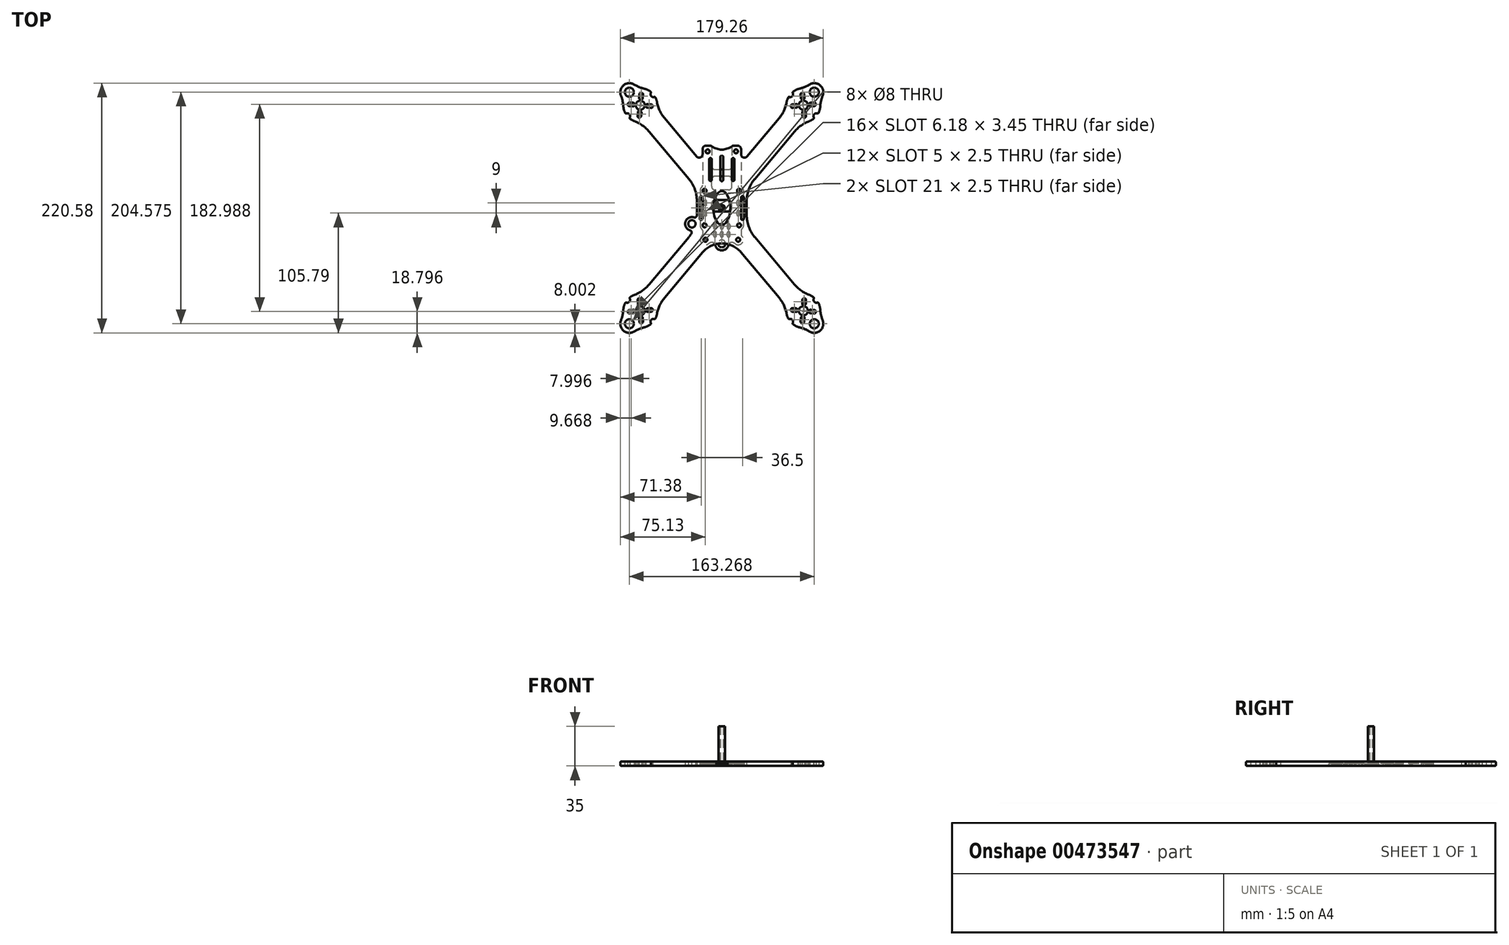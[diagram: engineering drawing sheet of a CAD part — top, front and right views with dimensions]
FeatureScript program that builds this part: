
annotation { "Feature Type Name" : "Feature", "Feature Type Description" : "" }
export const myFeature = defineFeature(function(context is Context, id is Id, definition is map)
    precondition{}
    {
        {
            var Q0;
            Q0=qCreatedBy(makeId("Top.planeOp"),FACE);
            var sketch = newSketch(context, id + "F0", { "sketchPlane" : qUnion([Q0])});
            skCircle(sketch, "E0", {"center": v(-72, 90.8) * mm, "radius": 64.25 * mm, "construction": true});
            skLineSegment(sketch, "E1", {"start": v(-72, 90.8) * mm, "end": v(0, 5) * mm, "construction": true});
            skCircle(sketch, "E2", {"center": v(-72, 90.8) * mm, "radius": 4 * mm});
            skArc(sketch, "E3", {"start": v(-86.97, 89.92) * mm, "mid": v(-86.48, 86.9) * mm, "end": v(-85.4, 84.06) * mm});
            skArc(sketch, "E4", {"start": v(-77.42, 109.09) * mm, "mid": v(-86.78, 108.42) * mm, "end": v(-89.06, 99.32) * mm});
            skLineSegment(sketch, "E5", {"start": v(-81.63, 102.29) * mm, "end": v(-72, 90.8) * mm, "construction": true});
            skPoint(sketch, "E6.visualSharp", {"position": v(-74.36, 105.6) * mm});
            skArc(sketch, "E6.filletArc", {"start": v(-77.42, 109.09) * mm, "mid": v(-73.12, 106.88) * mm, "end": v(-68.53, 105.4) * mm});
            skArc(sketch, "E7.MirrorCS", {"start": v(-89.06, 99.32) * mm, "mid": v(-87.64, 94.7) * mm, "end": v(-86.97, 89.92) * mm});
            skCircle(sketch, "E8", {"center": v(-81.63, 102.29) * mm, "radius": 4 * mm});
            skLineSegment(sketch, "E9", {"start": v(-72, 90.8) * mm, "end": v(-60.5, 100.44) * mm, "construction": true});
            skArc(sketch, "E10", {"start": v(-62.73, 101.57) * mm, "mid": v(-62.42, 98.83) * mm, "end": v(-59.78, 98.05) * mm});
            skArc(sketch, "E11.trimOffspring", {"start": v(-63.03, 102.82) * mm, "mid": v(-65.65, 104.39) * mm, "end": v(-68.53, 105.4) * mm});
            skArc(sketch, "E12.MirrorCS", {"start": v(-84.2, 83.55) * mm, "mid": v(-81.57, 82.76) * mm, "end": v(-81.25, 80.03) * mm});
            skArc(sketch, "E13.trimOffspring", {"start": v(-80.96, 78.77) * mm, "mid": v(-79.2, 77.64) * mm, "end": v(-77.3, 76.77) * mm});
            skPoint(sketch, "E14.visualSharp", {"position": v(-62.26, 102.21) * mm});
            skArc(sketch, "E14.filletArc", {"start": v(-62.73, 101.57) * mm, "mid": v(-62.65, 102.25) * mm, "end": v(-63.03, 102.82) * mm});
            skPoint(sketch, "E15.visualSharp", {"position": v(-59.06, 98.4) * mm});
            skArc(sketch, "E15.filletArc", {"start": v(-58.6, 97.54) * mm, "mid": v(-59.1, 98) * mm, "end": v(-59.78, 98.05) * mm});
            skPoint(sketch, "E16.visualSharp", {"position": v(-84.92, 83.2) * mm});
            skArc(sketch, "E16.filletArc", {"start": v(-85.4, 84.06) * mm, "mid": v(-84.9, 83.59) * mm, "end": v(-84.2, 83.55) * mm});
            skPoint(sketch, "E17.visualSharp", {"position": v(-81.72, 79.38) * mm});
            skArc(sketch, "E17.filletArc", {"start": v(-81.25, 80.03) * mm, "mid": v(-81.33, 79.34) * mm, "end": v(-80.96, 78.77) * mm});
            skCircle(sketch, "E18", {"center": v(-15.25, 15.25) * mm, "radius": 1.75 * mm});
            skCircle(sketch, "E19", {"center": v(-12.5, 50) * mm, "radius": 1.75 * mm});
            skLineSegment(sketch, "E20", {"start": v(-14, 55) * mm, "end": v(-10.52, 55) * mm});
            skArc(sketch, "E21", {"start": v(-8.76, 54.43) * mm, "mid": v(-4.6, 52.33) * mm, "end": v(0, 51.6) * mm});
            skLineSegment(sketch, "E22.bottom", {"start": v(-18.25, 10.5) * mm, "end": v(-18.25, 10.5) * mm});
            skLineSegment(sketch, "E22.top", {"start": v(-19.5, 0) * mm, "end": v(-17, 0) * mm, "construction": true});
            skLineSegment(sketch, "E22.left", {"start": v(-19.5, 9.25) * mm, "end": v(-19.5, 0) * mm});
            skLineSegment(sketch, "E22.right", {"start": v(-17, 9.25) * mm, "end": v(-17, 0) * mm});
            skLineSegment(sketch, "E23", {"start": v(0, 51.6) * mm, "end": v(0, 0) * mm, "construction": true});
            skPoint(sketch, "E24.visualSharp", {"position": v(-9.5, 55) * mm});
            skArc(sketch, "E24.filletArc", {"start": v(-8.76, 54.43) * mm, "mid": v(-9.6, 54.86) * mm, "end": v(-10.52, 55) * mm});
            skLineSegment(sketch, "E25", {"start": v(-64.12, 67.4) * mm, "end": v(-29.02, 25.58) * mm});
            skLineSegment(sketch, "E26.MirrorCS", {"start": v(-50.67, 79.38) * mm, "end": v(-22.3, 45.58) * mm});
            skArc(sketch, "E27.trimOffspring", {"start": v(-57.22, 93.42) * mm, "mid": v(-57.76, 95.53) * mm, "end": v(-58.6, 97.54) * mm});
            skPoint(sketch, "E28.visualSharp", {"position": v(-57.38, 87.39) * mm});
            skArc(sketch, "E28.filletArc", {"start": v(-57.22, 93.42) * mm, "mid": v(-54.87, 85.97) * mm, "end": v(-50.67, 79.38) * mm});
            skPoint(sketch, "E29.visualSharp", {"position": v(-71.17, 75.82) * mm});
            skArc(sketch, "E29.filletArc", {"start": v(-64.12, 67.4) * mm, "mid": v(-70.1, 72.94) * mm, "end": v(-77.3, 76.77) * mm});
            skLineSegment(sketch, "E30", {"start": v(-17, 52) * mm, "end": v(-17, 47.5) * mm});
            skPoint(sketch, "E31.visualSharp", {"position": v(-17, 55) * mm});
            skArc(sketch, "E31.filletArc", {"start": v(-14, 55) * mm, "mid": v(-16.12, 54.12) * mm, "end": v(-17, 52) * mm});
            skPoint(sketch, "E32.visualSharp", {"position": v(-17, 39.26) * mm});
            skArc(sketch, "E32.filletArc", {"start": v(-22.3, 45.58) * mm, "mid": v(-18.97, 44.68) * mm, "end": v(-17, 47.5) * mm});
            skLineSegment(sketch, "E33", {"start": v(-22, 6.3) * mm, "end": v(-22, 0) * mm});
            skPoint(sketch, "E34.visualSharp", {"position": v(-22, 17.22) * mm});
            skArc(sketch, "E34.filletArc", {"start": v(-22, 6.3) * mm, "mid": v(-23.8, 16.56) * mm, "end": v(-29.02, 25.58) * mm});
            skPoint(sketch, "E35.visualSharp", {"position": v(-19.5, 10.5) * mm});
            skArc(sketch, "E35.filletArc", {"start": v(-18.25, 10.5) * mm, "mid": v(-19.13, 10.13) * mm, "end": v(-19.5, 9.25) * mm});
            skPoint(sketch, "E36.visualSharp", {"position": v(-17, 10.5) * mm});
            skArc(sketch, "E36.filletArc", {"start": v(-17, 9.25) * mm, "mid": v(-17.37, 10.13) * mm, "end": v(-18.25, 10.5) * mm});
            skCircle(sketch, "E37.MirrorC", {"center": v(12.5, 50) * mm, "radius": 1.75 * mm});
            skCircle(sketch, "E38.MirrorC", {"center": v(15.25, 15.25) * mm, "radius": 1.75 * mm});
            skArc(sketch, "E39.MirrorCS", {"start": v(17, 9.25) * mm, "mid": v(17.37, 10.13) * mm, "end": v(18.25, 10.5) * mm});
            skArc(sketch, "E40.MirrorCS", {"start": v(18.25, 10.5) * mm, "mid": v(19.13, 10.13) * mm, "end": v(19.5, 9.25) * mm});
            skLineSegment(sketch, "E41.MirrorCS", {"start": v(18.25, 10.5) * mm, "end": v(18.25, 10.5) * mm});
            skPoint(sketch, "E42.MirrorP", {"position": v(17, 10.5) * mm});
            skPoint(sketch, "E43.MirrorP", {"position": v(19.5, 10.5) * mm});
            skLineSegment(sketch, "E44.MirrorCS", {"start": v(17, 9.25) * mm, "end": v(17, 0) * mm});
            skLineSegment(sketch, "E45.MirrorCS", {"start": v(19.5, 9.25) * mm, "end": v(19.5, 0) * mm});
            skArc(sketch, "E46.MirrorCS", {"start": v(22, 6.3) * mm, "mid": v(23.8, 16.56) * mm, "end": v(29.02, 25.58) * mm});
            skLineSegment(sketch, "E47.MirrorCS", {"start": v(22, 6.3) * mm, "end": v(22, 0) * mm});
            skLineSegment(sketch, "E48.MirrorCS", {"start": v(50.67, 79.38) * mm, "end": v(22.3, 45.58) * mm});
            skLineSegment(sketch, "E49.MirrorCS", {"start": v(64.12, 67.4) * mm, "end": v(29.02, 25.58) * mm});
            skArc(sketch, "E50.MirrorCS", {"start": v(57.22, 93.42) * mm, "mid": v(54.87, 85.97) * mm, "end": v(50.67, 79.38) * mm});
            skArc(sketch, "E51.MirrorCS", {"start": v(64.12, 67.4) * mm, "mid": v(70.1, 72.94) * mm, "end": v(77.3, 76.77) * mm});
            skArc(sketch, "E52.MirrorCS", {"start": v(80.96, 78.77) * mm, "mid": v(79.2, 77.64) * mm, "end": v(77.3, 76.77) * mm});
            skArc(sketch, "E53.MirrorCS", {"start": v(57.22, 93.42) * mm, "mid": v(57.76, 95.53) * mm, "end": v(58.6, 97.54) * mm});
            skArc(sketch, "E54.MirrorCS", {"start": v(84.2, 83.55) * mm, "mid": v(81.57, 82.76) * mm, "end": v(81.25, 80.03) * mm});
            skArc(sketch, "E55.MirrorCS", {"start": v(85.4, 84.06) * mm, "mid": v(84.9, 83.59) * mm, "end": v(84.2, 83.55) * mm});
            skArc(sketch, "E56.MirrorCS", {"start": v(81.25, 80.03) * mm, "mid": v(81.33, 79.34) * mm, "end": v(80.96, 78.77) * mm});
            skArc(sketch, "E57.MirrorCS", {"start": v(86.97, 89.92) * mm, "mid": v(86.48, 86.9) * mm, "end": v(85.4, 84.06) * mm});
            skArc(sketch, "E58.MirrorCS", {"start": v(89.06, 99.32) * mm, "mid": v(87.64, 94.7) * mm, "end": v(86.97, 89.92) * mm});
            skArc(sketch, "E59.MirrorCS", {"start": v(77.42, 109.09) * mm, "mid": v(86.78, 108.42) * mm, "end": v(89.06, 99.32) * mm});
            skArc(sketch, "E60.MirrorCS", {"start": v(77.42, 109.09) * mm, "mid": v(73.12, 106.88) * mm, "end": v(68.53, 105.4) * mm});
            skArc(sketch, "E61.MirrorCS", {"start": v(63.03, 102.82) * mm, "mid": v(65.65, 104.39) * mm, "end": v(68.53, 105.4) * mm});
            skArc(sketch, "E62.MirrorCS", {"start": v(62.73, 101.57) * mm, "mid": v(62.65, 102.25) * mm, "end": v(63.03, 102.82) * mm});
            skArc(sketch, "E63.MirrorCS", {"start": v(62.73, 101.57) * mm, "mid": v(62.42, 98.83) * mm, "end": v(59.78, 98.05) * mm});
            skPoint(sketch, "E64.MirrorP", {"position": v(59.06, 98.4) * mm});
            skArc(sketch, "E65.MirrorCS", {"start": v(58.6, 97.54) * mm, "mid": v(59.1, 98) * mm, "end": v(59.78, 98.05) * mm});
            skCircle(sketch, "E66.MirrorC", {"center": v(81.63, 102.29) * mm, "radius": 4 * mm});
            skCircle(sketch, "E67.MirrorC", {"center": v(72, 90.8) * mm, "radius": 4 * mm});
            skArc(sketch, "E68.MirrorCS", {"start": v(22.3, 45.58) * mm, "mid": v(18.97, 44.68) * mm, "end": v(17, 47.5) * mm});
            skLineSegment(sketch, "E69.MirrorCS", {"start": v(17, 52) * mm, "end": v(17, 47.5) * mm});
            skArc(sketch, "E70.MirrorCS", {"start": v(14, 55) * mm, "mid": v(16.12, 54.12) * mm, "end": v(17, 52) * mm});
            skLineSegment(sketch, "E71.MirrorCS", {"start": v(14, 55) * mm, "end": v(10.52, 55) * mm});
            skArc(sketch, "E72.MirrorCS", {"start": v(8.76, 54.43) * mm, "mid": v(9.6, 54.86) * mm, "end": v(10.52, 55) * mm});
            skArc(sketch, "E73.MirrorCS", {"start": v(8.76, 54.43) * mm, "mid": v(4.6, 52.33) * mm, "end": v(0, 51.6) * mm});
            skArc(sketch, "E74.MirrorCS", {"start": v(58.6, -97.54) * mm, "mid": v(59.1, -98) * mm, "end": v(59.78, -98.05) * mm});
            skArc(sketch, "E75.MirrorCS", {"start": v(81.25, -80.03) * mm, "mid": v(81.33, -79.34) * mm, "end": v(80.96, -78.77) * mm});
            skArc(sketch, "E76.MirrorCS", {"start": v(62.73, -101.57) * mm, "mid": v(62.65, -102.25) * mm, "end": v(63.03, -102.82) * mm});
            skArc(sketch, "E77.MirrorCS", {"start": v(85.4, -84.06) * mm, "mid": v(84.9, -83.59) * mm, "end": v(84.2, -83.55) * mm});
            skArc(sketch, "E78.MirrorCS", {"start": v(62.73, -101.57) * mm, "mid": v(62.42, -98.83) * mm, "end": v(59.78, -98.05) * mm});
            skArc(sketch, "E79.MirrorCS", {"start": v(80.96, -78.77) * mm, "mid": v(79.2, -77.64) * mm, "end": v(77.3, -76.77) * mm});
            skArc(sketch, "E80.MirrorCS", {"start": v(86.97, -89.92) * mm, "mid": v(86.48, -86.9) * mm, "end": v(85.4, -84.06) * mm});
            skArc(sketch, "E81.MirrorCS", {"start": v(77.42, -109.09) * mm, "mid": v(73.12, -106.88) * mm, "end": v(68.53, -105.4) * mm});
            skArc(sketch, "E82.MirrorCS", {"start": v(63.03, -102.82) * mm, "mid": v(65.65, -104.39) * mm, "end": v(68.53, -105.4) * mm});
            skArc(sketch, "E83.MirrorCS", {"start": v(84.2, -83.55) * mm, "mid": v(81.57, -82.76) * mm, "end": v(81.25, -80.03) * mm});
            skArc(sketch, "E84.MirrorCS", {"start": v(77.42, -109.09) * mm, "mid": v(86.78, -108.42) * mm, "end": v(89.06, -99.32) * mm});
            skArc(sketch, "E85.MirrorCS", {"start": v(57.22, -93.42) * mm, "mid": v(57.76, -95.53) * mm, "end": v(58.6, -97.54) * mm});
            skArc(sketch, "E86.MirrorCS", {"start": v(89.06, -99.32) * mm, "mid": v(87.64, -94.7) * mm, "end": v(86.97, -89.92) * mm});
            skCircle(sketch, "E87.MirrorC", {"center": v(72, -90.8) * mm, "radius": 4 * mm});
            skPoint(sketch, "E88.MirrorP", {"position": v(59.06, -98.4) * mm});
            skArc(sketch, "E89.MirrorCS", {"start": v(64.12, -67.4) * mm, "mid": v(70.1, -72.94) * mm, "end": v(77.3, -76.77) * mm});
            skCircle(sketch, "E90.MirrorC", {"center": v(81.63, -102.29) * mm, "radius": 4 * mm});
            skArc(sketch, "E91.MirrorCS", {"start": v(57.22, -93.42) * mm, "mid": v(54.87, -85.97) * mm, "end": v(50.67, -79.38) * mm});
            skArc(sketch, "E92.MirrorCS", {"start": v(-81.25, -80.03) * mm, "mid": v(-81.33, -79.34) * mm, "end": v(-80.96, -78.77) * mm});
            skArc(sketch, "E93.MirrorCS", {"start": v(-85.4, -84.06) * mm, "mid": v(-84.9, -83.59) * mm, "end": v(-84.2, -83.55) * mm});
            skArc(sketch, "E94.MirrorCS", {"start": v(-58.6, -97.54) * mm, "mid": v(-59.1, -98) * mm, "end": v(-59.78, -98.05) * mm});
            skArc(sketch, "E95.MirrorCS", {"start": v(-62.73, -101.57) * mm, "mid": v(-62.65, -102.25) * mm, "end": v(-63.03, -102.82) * mm});
            skArc(sketch, "E96.MirrorCS", {"start": v(-80.96, -78.77) * mm, "mid": v(-79.2, -77.64) * mm, "end": v(-77.3, -76.77) * mm});
            skArc(sketch, "E97.MirrorCS", {"start": v(-57.22, -93.42) * mm, "mid": v(-57.76, -95.53) * mm, "end": v(-58.6, -97.54) * mm});
            skPoint(sketch, "E98.MirrorP", {"position": v(-81.72, -79.38) * mm});
            skArc(sketch, "E99.MirrorCS", {"start": v(-57.22, -93.42) * mm, "mid": v(-54.87, -85.97) * mm, "end": v(-50.67, -79.38) * mm});
            skCircle(sketch, "E100.MirrorC", {"center": v(-72, -90.8) * mm, "radius": 4 * mm});
            skArc(sketch, "E101.MirrorCS", {"start": v(-86.97, -89.92) * mm, "mid": v(-86.48, -86.9) * mm, "end": v(-85.4, -84.06) * mm});
            skArc(sketch, "E102.MirrorCS", {"start": v(-77.42, -109.09) * mm, "mid": v(-86.78, -108.42) * mm, "end": v(-89.06, -99.32) * mm});
            skPoint(sketch, "E103.MirrorP", {"position": v(-59.06, -98.4) * mm});
            skPoint(sketch, "E104.MirrorP", {"position": v(-57.38, -87.39) * mm});
            skArc(sketch, "E105.MirrorCS", {"start": v(-62.73, -101.57) * mm, "mid": v(-62.42, -98.83) * mm, "end": v(-59.78, -98.05) * mm});
            skArc(sketch, "E106.MirrorCS", {"start": v(-89.06, -99.32) * mm, "mid": v(-87.64, -94.7) * mm, "end": v(-86.97, -89.92) * mm});
            skLineSegment(sketch, "E107.MirrorCS", {"start": v(-81.63, -102.29) * mm, "end": v(-72, -90.8) * mm, "construction": true});
            skArc(sketch, "E108.MirrorCS", {"start": v(-77.42, -109.09) * mm, "mid": v(-73.12, -106.88) * mm, "end": v(-68.53, -105.4) * mm});
            skCircle(sketch, "E109.MirrorC", {"center": v(-81.63, -102.29) * mm, "radius": 4 * mm});
            skLineSegment(sketch, "E110.MirrorCS", {"start": v(-72, -90.8) * mm, "end": v(-60.5, -100.44) * mm, "construction": true});
            skArc(sketch, "E111.MirrorCS", {"start": v(-63.03, -102.82) * mm, "mid": v(-65.65, -104.39) * mm, "end": v(-68.53, -105.4) * mm});
            skPoint(sketch, "E112.MirrorP", {"position": v(-74.36, -105.6) * mm});
            skArc(sketch, "E113.MirrorCS", {"start": v(-84.2, -83.55) * mm, "mid": v(-81.57, -82.76) * mm, "end": v(-81.25, -80.03) * mm});
            skPoint(sketch, "E114.MirrorP", {"position": v(-71.17, -75.82) * mm});
            skPoint(sketch, "E115.MirrorP", {"position": v(-84.92, -83.2) * mm});
            skPoint(sketch, "E116.MirrorP", {"position": v(-62.26, -102.21) * mm});
            skArc(sketch, "E117.MirrorCS", {"start": v(-64.12, -67.4) * mm, "mid": v(-70.1, -72.94) * mm, "end": v(-77.3, -76.77) * mm});
            skLineSegment(sketch, "E118.MirrorCS", {"start": v(-64.12, -67.4) * mm, "end": v(-29.02, -25.58) * mm});
            skLineSegment(sketch, "E119.MirrorCS", {"start": v(64.12, -67.4) * mm, "end": v(29.02, -25.58) * mm});
            skArc(sketch, "E120.MirrorCS", {"start": v(-22, -6.3) * mm, "mid": v(-22, -6.33) * mm, "end": v(-22, -6.37) * mm});
            skArc(sketch, "E121.MirrorCS", {"start": v(22, -6.3) * mm, "mid": v(23.8, -16.56) * mm, "end": v(29.02, -25.58) * mm});
            skCircle(sketch, "E122.MirrorC", {"center": v(-15.25, -15.25) * mm, "radius": 1.75 * mm});
            skCircle(sketch, "E123.MirrorC", {"center": v(15.25, -15.25) * mm, "radius": 1.75 * mm});
            skPoint(sketch, "E124.MirrorP", {"position": v(-19.5, -10.5) * mm});
            skPoint(sketch, "E125.MirrorP", {"position": v(-17, -10.5) * mm});
            skLineSegment(sketch, "E126.MirrorCS", {"start": v(-18.25, -10.5) * mm, "end": v(-18.25, -10.5) * mm});
            skLineSegment(sketch, "E127.MirrorCS", {"start": v(-19.5, -9.25) * mm, "end": v(-19.5, 0) * mm});
            skLineSegment(sketch, "E128.MirrorCS", {"start": v(-17, -9.25) * mm, "end": v(-17, 0) * mm});
            skArc(sketch, "E129.MirrorCS", {"start": v(-18.25, -10.5) * mm, "mid": v(-19.13, -10.13) * mm, "end": v(-19.5, -9.25) * mm});
            skArc(sketch, "E130.MirrorCS", {"start": v(-17, -9.25) * mm, "mid": v(-17.37, -10.13) * mm, "end": v(-18.25, -10.5) * mm});
            skArc(sketch, "E131.MirrorCS", {"start": v(17, -9.25) * mm, "mid": v(17.37, -10.13) * mm, "end": v(18.25, -10.5) * mm});
            skLineSegment(sketch, "E132.MirrorCS", {"start": v(18.25, -10.5) * mm, "end": v(18.25, -10.5) * mm});
            skLineSegment(sketch, "E133.MirrorCS", {"start": v(19.5, -9.25) * mm, "end": v(19.5, 0) * mm});
            skPoint(sketch, "E134.MirrorP", {"position": v(19.5, -10.5) * mm});
            skArc(sketch, "E135.MirrorCS", {"start": v(18.25, -10.5) * mm, "mid": v(19.13, -10.13) * mm, "end": v(19.5, -9.25) * mm});
            skLineSegment(sketch, "E136.MirrorCS", {"start": v(17, -9.25) * mm, "end": v(17, 0) * mm});
            skPoint(sketch, "E137.MirrorP", {"position": v(17, -10.5) * mm});
            skLineSegment(sketch, "E138.MirrorCS", {"start": v(-22, -6.3) * mm, "end": v(-22, 0) * mm});
            skLineSegment(sketch, "E139.MirrorCS", {"start": v(22, -6.3) * mm, "end": v(22, 0) * mm});
            skCircle(sketch, "E140", {"center": v(-14.5, -28) * mm, "radius": 1.75 * mm});
            skCircle(sketch, "E141.MirrorC", {"center": v(14.5, -28) * mm, "radius": 1.75 * mm});
            skLineSegment(sketch, "E142", {"start": v(-50.67, -79.38) * mm, "end": v(-16.85, -39.09) * mm});
            skLineSegment(sketch, "E143", {"start": v(50.67, -79.38) * mm, "end": v(16.85, -39.09) * mm});
            skPoint(sketch, "E144.visualSharp", {"position": v(0, -19) * mm});
            skArc(sketch, "E144.filletArc", {"start": v(16.85, -39.09) * mm, "mid": v(0, -31.23) * mm, "end": v(-16.85, -39.09) * mm});
            skCircle(sketch, "E145.MirrorC", {"center": v(-72, -90.8) * mm, "radius": 64.25 * mm, "construction": true});
            skCircle(sketch, "E146", {"center": v(-26.38, -14) * mm, "radius": 3.25 * mm});
            skArc(sketch, "E147", {"start": v(-24.6, -8.27) * mm, "mid": v(-32.13, -12.27) * mm, "end": v(-28.05, -19.76) * mm});
            skArc(sketch, "E148.trimOffspring", {"start": v(-26.94, -22.78) * mm, "mid": v(-27.94, -24.21) * mm, "end": v(-29.02, -25.58) * mm});
            skPoint(sketch, "E149.visualSharp", {"position": v(-22.2, -9.7) * mm});
            skArc(sketch, "E149.filletArc", {"start": v(-24.6, -8.27) * mm, "mid": v(-22.82, -7.98) * mm, "end": v(-22, -6.37) * mm});
            skPoint(sketch, "E150.visualSharp", {"position": v(-25.26, -19.9) * mm});
            skArc(sketch, "E150.filletArc", {"start": v(-26.94, -22.78) * mm, "mid": v(-26.73, -21) * mm, "end": v(-28.05, -19.76) * mm});
            skSolve(sketch);
        }
        {
            var Q0;
            Q0=makeQuery(id+"F0.imprint","IMPRINT",FACE,{"disambiguationData":[TD([[makeQuery(id+"F0.imprint","IMPRINT",EDGE,{"derivedFrom":sQuery(id+"F0.wireOp",EDGE,"E2")}),-1.0]])]});
            extrude(context, id + "F1", {"entities" : qUnion([Q0]), "depth" : 4 * mm});
        }
        {
            var Q0;
            Q0=makeQuery(id+"F1.opExtrude","CAP_EDGE",EDGE,{"disambiguationData":[OSD([sQuery(id+"F0.wireOp",EDGE,"E28.filletArc")])],"isStart":false});
            var Q1;
            Q1=makeQuery(id+"F1.opExtrude","CAP_EDGE",EDGE,{"disambiguationData":[OSD([sQuery(id+"F0.wireOp",EDGE,"E59.MirrorCS")])],"isStart":true});
            fillet(context, id + "F2", {"entities" : qUnion([Q0, Q1]), "radius" : 1 * mm, "tangentPropagation" : true, "allowEdgeOverflow" : false});
        }
        {
            var Q0;
            Q0=makeQuery(id+"F1.opExtrude","CAP_FACE",FACE,{"disambiguationData":[OSD([sQuery(id+"F0.wireOp",EDGE,"E2"),sQuery(id+"F0.wireOp",EDGE,"E3"),sQuery(id+"F0.wireOp",EDGE,"E4"),sQuery(id+"F0.wireOp",EDGE,"E6.filletArc"),sQuery(id+"F0.wireOp",EDGE,"E7.MirrorCS"),sQuery(id+"F0.wireOp",EDGE,"E8"),sQuery(id+"F0.wireOp",EDGE,"E10"),sQuery(id+"F0.wireOp",EDGE,"E11.trimOffspring"),sQuery(id+"F0.wireOp",EDGE,"E12.MirrorCS"),sQuery(id+"F0.wireOp",EDGE,"E13.trimOffspring"),sQuery(id+"F0.wireOp",EDGE,"E14.filletArc"),sQuery(id+"F0.wireOp",EDGE,"E15.filletArc"),sQuery(id+"F0.wireOp",EDGE,"E16.filletArc"),sQuery(id+"F0.wireOp",EDGE,"E17.filletArc"),sQuery(id+"F0.wireOp",EDGE,"E18"),sQuery(id+"F0.wireOp",EDGE,"E19"),sQuery(id+"F0.wireOp",EDGE,"E20"),sQuery(id+"F0.wireOp",EDGE,"E21"),sQuery(id+"F0.wireOp",EDGE,"E22.left"),sQuery(id+"F0.wireOp",EDGE,"E22.right"),sQuery(id+"F0.wireOp",EDGE,"E24.filletArc"),sQuery(id+"F0.wireOp",EDGE,"E25"),sQuery(id+"F0.wireOp",EDGE,"E26.MirrorCS"),sQuery(id+"F0.wireOp",EDGE,"E27.trimOffspring"),sQuery(id+"F0.wireOp",EDGE,"E28.filletArc"),sQuery(id+"F0.wireOp",EDGE,"E29.filletArc"),sQuery(id+"F0.wireOp",EDGE,"E30"),sQuery(id+"F0.wireOp",EDGE,"E31.filletArc"),sQuery(id+"F0.wireOp",EDGE,"E32.filletArc"),sQuery(id+"F0.wireOp",EDGE,"E33"),sQuery(id+"F0.wireOp",EDGE,"E34.filletArc"),sQuery(id+"F0.wireOp",EDGE,"E35.filletArc"),sQuery(id+"F0.wireOp",EDGE,"E36.filletArc"),sQuery(id+"F0.wireOp",EDGE,"E37.MirrorC"),sQuery(id+"F0.wireOp",EDGE,"E38.MirrorC"),sQuery(id+"F0.wireOp",EDGE,"E39.MirrorCS"),sQuery(id+"F0.wireOp",EDGE,"E40.MirrorCS"),sQuery(id+"F0.wireOp",EDGE,"E44.MirrorCS"),sQuery(id+"F0.wireOp",EDGE,"E45.MirrorCS"),sQuery(id+"F0.wireOp",EDGE,"E46.MirrorCS"),sQuery(id+"F0.wireOp",EDGE,"E47.MirrorCS"),sQuery(id+"F0.wireOp",EDGE,"E48.MirrorCS"),sQuery(id+"F0.wireOp",EDGE,"E49.MirrorCS"),sQuery(id+"F0.wireOp",EDGE,"E50.MirrorCS"),sQuery(id+"F0.wireOp",EDGE,"E51.MirrorCS"),sQuery(id+"F0.wireOp",EDGE,"E52.MirrorCS"),sQuery(id+"F0.wireOp",EDGE,"E53.MirrorCS"),sQuery(id+"F0.wireOp",EDGE,"E54.MirrorCS"),sQuery(id+"F0.wireOp",EDGE,"E55.MirrorCS"),sQuery(id+"F0.wireOp",EDGE,"E56.MirrorCS"),sQuery(id+"F0.wireOp",EDGE,"E57.MirrorCS"),sQuery(id+"F0.wireOp",EDGE,"E58.MirrorCS"),sQuery(id+"F0.wireOp",EDGE,"E59.MirrorCS"),sQuery(id+"F0.wireOp",EDGE,"E60.MirrorCS"),sQuery(id+"F0.wireOp",EDGE,"E61.MirrorCS"),sQuery(id+"F0.wireOp",EDGE,"E62.MirrorCS"),sQuery(id+"F0.wireOp",EDGE,"E63.MirrorCS"),sQuery(id+"F0.wireOp",EDGE,"E65.MirrorCS"),sQuery(id+"F0.wireOp",EDGE,"E66.MirrorC"),sQuery(id+"F0.wireOp",EDGE,"E67.MirrorC"),sQuery(id+"F0.wireOp",EDGE,"E68.MirrorCS"),sQuery(id+"F0.wireOp",EDGE,"E69.MirrorCS"),sQuery(id+"F0.wireOp",EDGE,"E70.MirrorCS"),sQuery(id+"F0.wireOp",EDGE,"E71.MirrorCS"),sQuery(id+"F0.wireOp",EDGE,"E72.MirrorCS"),sQuery(id+"F0.wireOp",EDGE,"E73.MirrorCS"),sQuery(id+"F0.wireOp",EDGE,"E74.MirrorCS"),sQuery(id+"F0.wireOp",EDGE,"E75.MirrorCS"),sQuery(id+"F0.wireOp",EDGE,"E76.MirrorCS"),sQuery(id+"F0.wireOp",EDGE,"E77.MirrorCS"),sQuery(id+"F0.wireOp",EDGE,"E78.MirrorCS"),sQuery(id+"F0.wireOp",EDGE,"E79.MirrorCS"),sQuery(id+"F0.wireOp",EDGE,"E80.MirrorCS"),sQuery(id+"F0.wireOp",EDGE,"E81.MirrorCS"),sQuery(id+"F0.wireOp",EDGE,"E82.MirrorCS"),sQuery(id+"F0.wireOp",EDGE,"E83.MirrorCS"),sQuery(id+"F0.wireOp",EDGE,"E84.MirrorCS"),sQuery(id+"F0.wireOp",EDGE,"E85.MirrorCS"),sQuery(id+"F0.wireOp",EDGE,"E86.MirrorCS"),sQuery(id+"F0.wireOp",EDGE,"E87.MirrorC"),sQuery(id+"F0.wireOp",EDGE,"E89.MirrorCS"),sQuery(id+"F0.wireOp",EDGE,"E90.MirrorC"),sQuery(id+"F0.wireOp",EDGE,"E91.MirrorCS"),sQuery(id+"F0.wireOp",EDGE,"E92.MirrorCS"),sQuery(id+"F0.wireOp",EDGE,"E93.MirrorCS"),sQuery(id+"F0.wireOp",EDGE,"E94.MirrorCS"),sQuery(id+"F0.wireOp",EDGE,"E95.MirrorCS"),sQuery(id+"F0.wireOp",EDGE,"E96.MirrorCS"),sQuery(id+"F0.wireOp",EDGE,"E97.MirrorCS"),sQuery(id+"F0.wireOp",EDGE,"E99.MirrorCS"),sQuery(id+"F0.wireOp",EDGE,"E100.MirrorC"),sQuery(id+"F0.wireOp",EDGE,"E101.MirrorCS"),sQuery(id+"F0.wireOp",EDGE,"E102.MirrorCS"),sQuery(id+"F0.wireOp",EDGE,"E105.MirrorCS"),sQuery(id+"F0.wireOp",EDGE,"E106.MirrorCS"),sQuery(id+"F0.wireOp",EDGE,"E108.MirrorCS"),sQuery(id+"F0.wireOp",EDGE,"E109.MirrorC"),sQuery(id+"F0.wireOp",EDGE,"E111.MirrorCS"),sQuery(id+"F0.wireOp",EDGE,"E113.MirrorCS"),sQuery(id+"F0.wireOp",EDGE,"E117.MirrorCS"),sQuery(id+"F0.wireOp",EDGE,"E118.MirrorCS"),sQuery(id+"F0.wireOp",EDGE,"E119.MirrorCS"),sQuery(id+"F0.wireOp",EDGE,"E120.MirrorCS"),sQuery(id+"F0.wireOp",EDGE,"E121.MirrorCS"),sQuery(id+"F0.wireOp",EDGE,"E122.MirrorC"),sQuery(id+"F0.wireOp",EDGE,"E123.MirrorC"),sQuery(id+"F0.wireOp",EDGE,"E127.MirrorCS"),sQuery(id+"F0.wireOp",EDGE,"E128.MirrorCS"),sQuery(id+"F0.wireOp",EDGE,"E129.MirrorCS"),sQuery(id+"F0.wireOp",EDGE,"E130.MirrorCS"),sQuery(id+"F0.wireOp",EDGE,"E131.MirrorCS"),sQuery(id+"F0.wireOp",EDGE,"E133.MirrorCS"),sQuery(id+"F0.wireOp",EDGE,"E135.MirrorCS"),sQuery(id+"F0.wireOp",EDGE,"E136.MirrorCS"),sQuery(id+"F0.wireOp",EDGE,"E138.MirrorCS"),sQuery(id+"F0.wireOp",EDGE,"E139.MirrorCS"),sQuery(id+"F0.wireOp",EDGE,"E140"),sQuery(id+"F0.wireOp",EDGE,"E141.MirrorC"),sQuery(id+"F0.wireOp",EDGE,"E142"),sQuery(id+"F0.wireOp",EDGE,"E143"),sQuery(id+"F0.wireOp",EDGE,"E144.filletArc")])],"isStart":true});
            var sketch = newSketch(context, id + "F3", { "sketchPlane" : qUnion([Q0])});
            skLineSegment(sketch, "E151", {"start": v(-72, 90.8) * mm, "end": v(0, 5) * mm, "construction": true});
            skLineSegment(sketch, "E152", {"start": v(-72, 90.8) * mm, "end": v(-65.52, 90.23) * mm, "construction": true});
            skLineSegment(sketch, "E153", {"start": v(-65.52, 90.23) * mm, "end": v(-62.53, 89.97) * mm, "construction": true});
            skArc(sketch, "E154.0.startCap", {"start": v(-65.66, 88.64) * mm, "mid": v(-67.11, 90.37) * mm, "end": v(-65.38, 91.82) * mm});
            skArc(sketch, "E154.0.endCap", {"start": v(-62.39, 91.56) * mm, "mid": v(-60.93, 89.83) * mm, "end": v(-62.67, 88.38) * mm});
            skLineSegment(sketch, "E154.0.left", {"start": v(-65.38, 91.82) * mm, "end": v(-62.39, 91.56) * mm});
            skLineSegment(sketch, "E154.0.right", {"start": v(-65.66, 88.64) * mm, "end": v(-62.67, 88.38) * mm});
            skLineSegment(sketch, "E155.1.0", {"start": v(-73.02, 97.41) * mm, "end": v(-72.76, 100.4) * mm});
            skArc(sketch, "E155.1.1", {"start": v(-72.76, 100.4) * mm, "mid": v(-71.02, 101.85) * mm, "end": v(-69.57, 100.12) * mm});
            skLineSegment(sketch, "E155.1.2", {"start": v(-69.83, 97.13) * mm, "end": v(-69.57, 100.12) * mm});
            skArc(sketch, "E155.1.3", {"start": v(-69.83, 97.13) * mm, "mid": v(-71.57, 95.68) * mm, "end": v(-73.02, 97.41) * mm});
            skLineSegment(sketch, "E155.2.0", {"start": v(-78.6, 89.77) * mm, "end": v(-81.6, 90.03) * mm});
            skArc(sketch, "E155.2.1", {"start": v(-81.6, 90.03) * mm, "mid": v(-83.05, 91.76) * mm, "end": v(-81.32, 93.22) * mm});
            skLineSegment(sketch, "E155.2.2", {"start": v(-78.33, 92.96) * mm, "end": v(-81.32, 93.22) * mm});
            skArc(sketch, "E155.2.3", {"start": v(-78.33, 92.96) * mm, "mid": v(-76.87, 91.22) * mm, "end": v(-78.6, 89.77) * mm});
            skLineSegment(sketch, "E155.3.0", {"start": v(-70.96, 84.18) * mm, "end": v(-71.23, 81.2) * mm});
            skArc(sketch, "E155.3.1", {"start": v(-71.23, 81.2) * mm, "mid": v(-72.96, 79.74) * mm, "end": v(-74.41, 81.47) * mm});
            skLineSegment(sketch, "E155.3.2", {"start": v(-74.15, 84.46) * mm, "end": v(-74.41, 81.47) * mm});
            skArc(sketch, "E155.3.3", {"start": v(-74.15, 84.46) * mm, "mid": v(-72.42, 85.92) * mm, "end": v(-70.96, 84.18) * mm});
            skPoint(sketch, "E155.center", {"position": v(-72, 90.8) * mm});
            skLineSegment(sketch, "E156.MirrorCS", {"start": v(65.52, 90.23) * mm, "end": v(62.53, 89.97) * mm, "construction": true});
            skLineSegment(sketch, "E157.MirrorCS", {"start": v(65.66, 88.64) * mm, "end": v(62.67, 88.38) * mm});
            skArc(sketch, "E158.MirrorCS", {"start": v(62.39, 91.56) * mm, "mid": v(60.93, 89.83) * mm, "end": v(62.67, 88.38) * mm});
            skArc(sketch, "E159.MirrorCS", {"start": v(71.23, 81.2) * mm, "mid": v(72.96, 79.74) * mm, "end": v(74.41, 81.47) * mm});
            skArc(sketch, "E160.MirrorCS", {"start": v(81.6, 90.03) * mm, "mid": v(83.05, 91.76) * mm, "end": v(81.32, 93.22) * mm});
            skLineSegment(sketch, "E161.MirrorCS", {"start": v(78.6, 89.77) * mm, "end": v(81.6, 90.03) * mm});
            skArc(sketch, "E162.MirrorCS", {"start": v(69.83, 97.13) * mm, "mid": v(71.57, 95.68) * mm, "end": v(73.02, 97.41) * mm});
            skLineSegment(sketch, "E163.MirrorCS", {"start": v(69.83, 97.13) * mm, "end": v(69.57, 100.12) * mm});
            skArc(sketch, "E164.MirrorCS", {"start": v(72.76, 100.4) * mm, "mid": v(71.02, 101.85) * mm, "end": v(69.57, 100.12) * mm});
            skLineSegment(sketch, "E165.MirrorCS", {"start": v(70.96, 84.18) * mm, "end": v(71.23, 81.2) * mm});
            skArc(sketch, "E166.MirrorCS", {"start": v(65.66, 88.64) * mm, "mid": v(67.11, 90.37) * mm, "end": v(65.38, 91.82) * mm});
            skLineSegment(sketch, "E167.MirrorCS", {"start": v(73.02, 97.41) * mm, "end": v(72.76, 100.4) * mm});
            skLineSegment(sketch, "E168.MirrorCS", {"start": v(65.38, 91.82) * mm, "end": v(62.39, 91.56) * mm});
            skArc(sketch, "E169.MirrorCS", {"start": v(78.33, 92.96) * mm, "mid": v(76.87, 91.22) * mm, "end": v(78.6, 89.77) * mm});
            skArc(sketch, "E170.MirrorCS", {"start": v(74.15, 84.46) * mm, "mid": v(72.42, 85.92) * mm, "end": v(70.96, 84.18) * mm});
            skLineSegment(sketch, "E171.MirrorCS", {"start": v(78.33, 92.96) * mm, "end": v(81.32, 93.22) * mm});
            skLineSegment(sketch, "E172.MirrorCS", {"start": v(74.15, 84.46) * mm, "end": v(74.41, 81.47) * mm});
            skLineSegment(sketch, "E173.MirrorCS", {"start": v(72, 90.8) * mm, "end": v(65.52, 90.23) * mm, "construction": true});
            skPoint(sketch, "E174.MirrorP", {"position": v(72, 90.8) * mm});
            skArc(sketch, "E175.MirrorCS", {"start": v(65.66, -88.64) * mm, "mid": v(67.11, -90.37) * mm, "end": v(65.38, -91.82) * mm});
            skLineSegment(sketch, "E176.MirrorCS", {"start": v(65.66, -88.64) * mm, "end": v(62.67, -88.38) * mm});
            skLineSegment(sketch, "E177.MirrorCS", {"start": v(65.52, -90.23) * mm, "end": v(62.53, -89.97) * mm, "construction": true});
            skLineSegment(sketch, "E178.MirrorCS", {"start": v(-65.66, -88.64) * mm, "end": v(-62.67, -88.38) * mm});
            skLineSegment(sketch, "E179.MirrorCS", {"start": v(-65.38, -91.82) * mm, "end": v(-62.39, -91.56) * mm});
            skLineSegment(sketch, "E180.MirrorCS", {"start": v(65.38, -91.82) * mm, "end": v(62.39, -91.56) * mm});
            skArc(sketch, "E181.MirrorCS", {"start": v(-65.66, -88.64) * mm, "mid": v(-67.11, -90.37) * mm, "end": v(-65.38, -91.82) * mm});
            skLineSegment(sketch, "E182.MirrorCS", {"start": v(-65.52, -90.23) * mm, "end": v(-62.53, -89.97) * mm, "construction": true});
            skArc(sketch, "E183.MirrorCS", {"start": v(-62.39, -91.56) * mm, "mid": v(-60.93, -89.83) * mm, "end": v(-62.67, -88.38) * mm});
            skArc(sketch, "E184.MirrorCS", {"start": v(-74.15, -84.46) * mm, "mid": v(-72.42, -85.92) * mm, "end": v(-70.96, -84.18) * mm});
            skLineSegment(sketch, "E185.MirrorCS", {"start": v(-70.96, -84.18) * mm, "end": v(-71.23, -81.2) * mm});
            skArc(sketch, "E186.MirrorCS", {"start": v(62.39, -91.56) * mm, "mid": v(60.93, -89.83) * mm, "end": v(62.67, -88.38) * mm});
            skLineSegment(sketch, "E187.MirrorCS", {"start": v(78.6, -89.77) * mm, "end": v(81.6, -90.03) * mm});
            skLineSegment(sketch, "E188.MirrorCS", {"start": v(-72, -90.8) * mm, "end": v(-65.52, -90.23) * mm, "construction": true});
            skLineSegment(sketch, "E189.MirrorCS", {"start": v(72, -90.8) * mm, "end": v(65.52, -90.23) * mm, "construction": true});
            skArc(sketch, "E190.MirrorCS", {"start": v(72.76, -100.4) * mm, "mid": v(71.02, -101.85) * mm, "end": v(69.57, -100.12) * mm});
            skLineSegment(sketch, "E191.MirrorCS", {"start": v(74.15, -84.46) * mm, "end": v(74.41, -81.47) * mm});
            skLineSegment(sketch, "E192.MirrorCS", {"start": v(69.83, -97.13) * mm, "end": v(69.57, -100.12) * mm});
            skArc(sketch, "E193.MirrorCS", {"start": v(-81.6, -90.03) * mm, "mid": v(-83.05, -91.76) * mm, "end": v(-81.32, -93.22) * mm});
            skLineSegment(sketch, "E194.MirrorCS", {"start": v(-78.6, -89.77) * mm, "end": v(-81.6, -90.03) * mm});
            skArc(sketch, "E195.MirrorCS", {"start": v(-69.83, -97.13) * mm, "mid": v(-71.57, -95.68) * mm, "end": v(-73.02, -97.41) * mm});
            skLineSegment(sketch, "E196.MirrorCS", {"start": v(-69.83, -97.13) * mm, "end": v(-69.57, -100.12) * mm});
            skArc(sketch, "E197.MirrorCS", {"start": v(-72.76, -100.4) * mm, "mid": v(-71.02, -101.85) * mm, "end": v(-69.57, -100.12) * mm});
            skLineSegment(sketch, "E198.MirrorCS", {"start": v(-73.02, -97.41) * mm, "end": v(-72.76, -100.4) * mm});
            skLineSegment(sketch, "E199.MirrorCS", {"start": v(70.96, -84.18) * mm, "end": v(71.23, -81.2) * mm});
            skLineSegment(sketch, "E200.MirrorCS", {"start": v(73.02, -97.41) * mm, "end": v(72.76, -100.4) * mm});
            skArc(sketch, "E201.MirrorCS", {"start": v(71.23, -81.2) * mm, "mid": v(72.96, -79.74) * mm, "end": v(74.41, -81.47) * mm});
            skLineSegment(sketch, "E202.MirrorCS", {"start": v(-74.15, -84.46) * mm, "end": v(-74.41, -81.47) * mm});
            skArc(sketch, "E203.MirrorCS", {"start": v(78.33, -92.96) * mm, "mid": v(76.87, -91.22) * mm, "end": v(78.6, -89.77) * mm});
            skArc(sketch, "E204.MirrorCS", {"start": v(81.6, -90.03) * mm, "mid": v(83.05, -91.76) * mm, "end": v(81.32, -93.22) * mm});
            skArc(sketch, "E205.MirrorCS", {"start": v(74.15, -84.46) * mm, "mid": v(72.42, -85.92) * mm, "end": v(70.96, -84.18) * mm});
            skArc(sketch, "E206.MirrorCS", {"start": v(-78.33, -92.96) * mm, "mid": v(-76.87, -91.22) * mm, "end": v(-78.6, -89.77) * mm});
            skArc(sketch, "E207.MirrorCS", {"start": v(-71.23, -81.2) * mm, "mid": v(-72.96, -79.74) * mm, "end": v(-74.41, -81.47) * mm});
            skLineSegment(sketch, "E208.MirrorCS", {"start": v(78.33, -92.96) * mm, "end": v(81.32, -93.22) * mm});
            skLineSegment(sketch, "E209.MirrorCS", {"start": v(-78.33, -92.96) * mm, "end": v(-81.32, -93.22) * mm});
            skArc(sketch, "E210.MirrorCS", {"start": v(69.83, -97.13) * mm, "mid": v(71.57, -95.68) * mm, "end": v(73.02, -97.41) * mm});
            skPoint(sketch, "E211.MirrorP", {"position": v(72, -90.8) * mm});
            skPoint(sketch, "E212.MirrorP", {"position": v(-72, -90.8) * mm});
            skSolve(sketch);
        }
        {
            var Q0;
            Q0 = qSketchRegion(id + "F3", true);
            extrude(context, id + "F4", {"entities" : qUnion([Q0]), "operationType" : NewBodyOperationType.REMOVE, "oppositeDirection" : true, "depth" : 25 * mm});
        }
        {
            var Q0;
            Q0=makeQuery(id+"F1.opExtrude","CAP_FACE",FACE,{"disambiguationData":[OSD([sQuery(id+"F0.wireOp",EDGE,"E2"),sQuery(id+"F0.wireOp",EDGE,"E3"),sQuery(id+"F0.wireOp",EDGE,"E4"),sQuery(id+"F0.wireOp",EDGE,"E6.filletArc"),sQuery(id+"F0.wireOp",EDGE,"E7.MirrorCS"),sQuery(id+"F0.wireOp",EDGE,"E8"),sQuery(id+"F0.wireOp",EDGE,"E10"),sQuery(id+"F0.wireOp",EDGE,"E11.trimOffspring"),sQuery(id+"F0.wireOp",EDGE,"E12.MirrorCS"),sQuery(id+"F0.wireOp",EDGE,"E13.trimOffspring"),sQuery(id+"F0.wireOp",EDGE,"E14.filletArc"),sQuery(id+"F0.wireOp",EDGE,"E15.filletArc"),sQuery(id+"F0.wireOp",EDGE,"E16.filletArc"),sQuery(id+"F0.wireOp",EDGE,"E17.filletArc"),sQuery(id+"F0.wireOp",EDGE,"E18"),sQuery(id+"F0.wireOp",EDGE,"E19"),sQuery(id+"F0.wireOp",EDGE,"E20"),sQuery(id+"F0.wireOp",EDGE,"E21"),sQuery(id+"F0.wireOp",EDGE,"E22.left"),sQuery(id+"F0.wireOp",EDGE,"E22.right"),sQuery(id+"F0.wireOp",EDGE,"E24.filletArc"),sQuery(id+"F0.wireOp",EDGE,"E25"),sQuery(id+"F0.wireOp",EDGE,"E26.MirrorCS"),sQuery(id+"F0.wireOp",EDGE,"E27.trimOffspring"),sQuery(id+"F0.wireOp",EDGE,"E28.filletArc"),sQuery(id+"F0.wireOp",EDGE,"E29.filletArc"),sQuery(id+"F0.wireOp",EDGE,"E30"),sQuery(id+"F0.wireOp",EDGE,"E31.filletArc"),sQuery(id+"F0.wireOp",EDGE,"E32.filletArc"),sQuery(id+"F0.wireOp",EDGE,"E33"),sQuery(id+"F0.wireOp",EDGE,"E34.filletArc"),sQuery(id+"F0.wireOp",EDGE,"E35.filletArc"),sQuery(id+"F0.wireOp",EDGE,"E36.filletArc"),sQuery(id+"F0.wireOp",EDGE,"E37.MirrorC"),sQuery(id+"F0.wireOp",EDGE,"E38.MirrorC"),sQuery(id+"F0.wireOp",EDGE,"E39.MirrorCS"),sQuery(id+"F0.wireOp",EDGE,"E40.MirrorCS"),sQuery(id+"F0.wireOp",EDGE,"E44.MirrorCS"),sQuery(id+"F0.wireOp",EDGE,"E45.MirrorCS"),sQuery(id+"F0.wireOp",EDGE,"E46.MirrorCS"),sQuery(id+"F0.wireOp",EDGE,"E47.MirrorCS"),sQuery(id+"F0.wireOp",EDGE,"E48.MirrorCS"),sQuery(id+"F0.wireOp",EDGE,"E49.MirrorCS"),sQuery(id+"F0.wireOp",EDGE,"E50.MirrorCS"),sQuery(id+"F0.wireOp",EDGE,"E51.MirrorCS"),sQuery(id+"F0.wireOp",EDGE,"E52.MirrorCS"),sQuery(id+"F0.wireOp",EDGE,"E53.MirrorCS"),sQuery(id+"F0.wireOp",EDGE,"E54.MirrorCS"),sQuery(id+"F0.wireOp",EDGE,"E55.MirrorCS"),sQuery(id+"F0.wireOp",EDGE,"E56.MirrorCS"),sQuery(id+"F0.wireOp",EDGE,"E57.MirrorCS"),sQuery(id+"F0.wireOp",EDGE,"E58.MirrorCS"),sQuery(id+"F0.wireOp",EDGE,"E59.MirrorCS"),sQuery(id+"F0.wireOp",EDGE,"E60.MirrorCS"),sQuery(id+"F0.wireOp",EDGE,"E61.MirrorCS"),sQuery(id+"F0.wireOp",EDGE,"E62.MirrorCS"),sQuery(id+"F0.wireOp",EDGE,"E63.MirrorCS"),sQuery(id+"F0.wireOp",EDGE,"E65.MirrorCS"),sQuery(id+"F0.wireOp",EDGE,"E66.MirrorC"),sQuery(id+"F0.wireOp",EDGE,"E67.MirrorC"),sQuery(id+"F0.wireOp",EDGE,"E68.MirrorCS"),sQuery(id+"F0.wireOp",EDGE,"E69.MirrorCS"),sQuery(id+"F0.wireOp",EDGE,"E70.MirrorCS"),sQuery(id+"F0.wireOp",EDGE,"E71.MirrorCS"),sQuery(id+"F0.wireOp",EDGE,"E72.MirrorCS"),sQuery(id+"F0.wireOp",EDGE,"E73.MirrorCS"),sQuery(id+"F0.wireOp",EDGE,"E74.MirrorCS"),sQuery(id+"F0.wireOp",EDGE,"E75.MirrorCS"),sQuery(id+"F0.wireOp",EDGE,"E76.MirrorCS"),sQuery(id+"F0.wireOp",EDGE,"E77.MirrorCS"),sQuery(id+"F0.wireOp",EDGE,"E78.MirrorCS"),sQuery(id+"F0.wireOp",EDGE,"E79.MirrorCS"),sQuery(id+"F0.wireOp",EDGE,"E80.MirrorCS"),sQuery(id+"F0.wireOp",EDGE,"E81.MirrorCS"),sQuery(id+"F0.wireOp",EDGE,"E82.MirrorCS"),sQuery(id+"F0.wireOp",EDGE,"E83.MirrorCS"),sQuery(id+"F0.wireOp",EDGE,"E84.MirrorCS"),sQuery(id+"F0.wireOp",EDGE,"E85.MirrorCS"),sQuery(id+"F0.wireOp",EDGE,"E86.MirrorCS"),sQuery(id+"F0.wireOp",EDGE,"E87.MirrorC"),sQuery(id+"F0.wireOp",EDGE,"E89.MirrorCS"),sQuery(id+"F0.wireOp",EDGE,"E90.MirrorC"),sQuery(id+"F0.wireOp",EDGE,"E91.MirrorCS"),sQuery(id+"F0.wireOp",EDGE,"E92.MirrorCS"),sQuery(id+"F0.wireOp",EDGE,"E93.MirrorCS"),sQuery(id+"F0.wireOp",EDGE,"E94.MirrorCS"),sQuery(id+"F0.wireOp",EDGE,"E95.MirrorCS"),sQuery(id+"F0.wireOp",EDGE,"E96.MirrorCS"),sQuery(id+"F0.wireOp",EDGE,"E97.MirrorCS"),sQuery(id+"F0.wireOp",EDGE,"E99.MirrorCS"),sQuery(id+"F0.wireOp",EDGE,"E100.MirrorC"),sQuery(id+"F0.wireOp",EDGE,"E101.MirrorCS"),sQuery(id+"F0.wireOp",EDGE,"E102.MirrorCS"),sQuery(id+"F0.wireOp",EDGE,"E105.MirrorCS"),sQuery(id+"F0.wireOp",EDGE,"E106.MirrorCS"),sQuery(id+"F0.wireOp",EDGE,"E108.MirrorCS"),sQuery(id+"F0.wireOp",EDGE,"E109.MirrorC"),sQuery(id+"F0.wireOp",EDGE,"E111.MirrorCS"),sQuery(id+"F0.wireOp",EDGE,"E113.MirrorCS"),sQuery(id+"F0.wireOp",EDGE,"E117.MirrorCS"),sQuery(id+"F0.wireOp",EDGE,"E118.MirrorCS"),sQuery(id+"F0.wireOp",EDGE,"E119.MirrorCS"),sQuery(id+"F0.wireOp",EDGE,"E120.MirrorCS"),sQuery(id+"F0.wireOp",EDGE,"E121.MirrorCS"),sQuery(id+"F0.wireOp",EDGE,"E122.MirrorC"),sQuery(id+"F0.wireOp",EDGE,"E123.MirrorC"),sQuery(id+"F0.wireOp",EDGE,"E127.MirrorCS"),sQuery(id+"F0.wireOp",EDGE,"E128.MirrorCS"),sQuery(id+"F0.wireOp",EDGE,"E129.MirrorCS"),sQuery(id+"F0.wireOp",EDGE,"E130.MirrorCS"),sQuery(id+"F0.wireOp",EDGE,"E131.MirrorCS"),sQuery(id+"F0.wireOp",EDGE,"E133.MirrorCS"),sQuery(id+"F0.wireOp",EDGE,"E135.MirrorCS"),sQuery(id+"F0.wireOp",EDGE,"E136.MirrorCS"),sQuery(id+"F0.wireOp",EDGE,"E138.MirrorCS"),sQuery(id+"F0.wireOp",EDGE,"E139.MirrorCS"),sQuery(id+"F0.wireOp",EDGE,"E140"),sQuery(id+"F0.wireOp",EDGE,"E141.MirrorC"),sQuery(id+"F0.wireOp",EDGE,"E142"),sQuery(id+"F0.wireOp",EDGE,"E143"),sQuery(id+"F0.wireOp",EDGE,"E144.filletArc")])],"isStart":true});
            var sketch = newSketch(context, id + "F5", { "sketchPlane" : qUnion([Q0])});
            skLineSegment(sketch, "E213", {"start": v(0, -25) * mm, "end": v(0, -45) * mm, "construction": true});
            skArc(sketch, "E214.0.startCap", {"start": v(-1.3, -25) * mm, "mid": v(0, -23.7) * mm, "end": v(1.3, -25) * mm});
            skArc(sketch, "E214.0.endCap", {"start": v(1.3, -45) * mm, "mid": v(0, -46.3) * mm, "end": v(-1.3, -45) * mm});
            skLineSegment(sketch, "E214.0.left", {"start": v(1.3, -25) * mm, "end": v(1.3, -45) * mm});
            skLineSegment(sketch, "E214.0.right", {"start": v(-1.3, -25) * mm, "end": v(-1.3, -45) * mm});
            skLineSegment(sketch, "E215", {"start": v(-10, -43) * mm, "end": v(-10, -25) * mm, "construction": true});
            skArc(sketch, "E216.0.startCap", {"start": v(-8.85, -43) * mm, "mid": v(-10, -44.15) * mm, "end": v(-11.15, -43) * mm});
            skArc(sketch, "E216.0.endCap", {"start": v(-11.15, -25) * mm, "mid": v(-10, -23.85) * mm, "end": v(-8.85, -25) * mm});
            skLineSegment(sketch, "E216.0.left", {"start": v(-11.15, -43) * mm, "end": v(-11.15, -25) * mm});
            skLineSegment(sketch, "E216.0.right", {"start": v(-8.85, -43) * mm, "end": v(-8.85, -25) * mm});
            skArc(sketch, "E217.MirrorCS", {"start": v(11.15, -25) * mm, "mid": v(10, -23.85) * mm, "end": v(8.85, -25) * mm});
            skLineSegment(sketch, "E218.MirrorCS", {"start": v(10, -43) * mm, "end": v(10, -25) * mm, "construction": true});
            skLineSegment(sketch, "E219.MirrorCS", {"start": v(11.15, -43) * mm, "end": v(11.15, -25) * mm});
            skLineSegment(sketch, "E220.MirrorCS", {"start": v(8.85, -43) * mm, "end": v(8.85, -25) * mm});
            skArc(sketch, "E221.MirrorCS", {"start": v(8.85, -43) * mm, "mid": v(10, -44.15) * mm, "end": v(11.15, -43) * mm});
            skSolve(sketch);
        }
        {
            var Q0;
            Q0 = qSketchRegion(id + "F5", true);
            extrude(context, id + "F6", {"entities" : qUnion([Q0]), "operationType" : NewBodyOperationType.REMOVE, "oppositeDirection" : true, "depth" : 25 * mm});
        }
        {
            var Q0;
            Q0=makeQuery(id+"F1.opExtrude","CAP_FACE",FACE,{"disambiguationData":[OSD([sQuery(id+"F0.wireOp",EDGE,"E2"),sQuery(id+"F0.wireOp",EDGE,"E3"),sQuery(id+"F0.wireOp",EDGE,"E4"),sQuery(id+"F0.wireOp",EDGE,"E6.filletArc"),sQuery(id+"F0.wireOp",EDGE,"E7.MirrorCS"),sQuery(id+"F0.wireOp",EDGE,"E8"),sQuery(id+"F0.wireOp",EDGE,"E10"),sQuery(id+"F0.wireOp",EDGE,"E11.trimOffspring"),sQuery(id+"F0.wireOp",EDGE,"E12.MirrorCS"),sQuery(id+"F0.wireOp",EDGE,"E13.trimOffspring"),sQuery(id+"F0.wireOp",EDGE,"E14.filletArc"),sQuery(id+"F0.wireOp",EDGE,"E15.filletArc"),sQuery(id+"F0.wireOp",EDGE,"E16.filletArc"),sQuery(id+"F0.wireOp",EDGE,"E17.filletArc"),sQuery(id+"F0.wireOp",EDGE,"E18"),sQuery(id+"F0.wireOp",EDGE,"E19"),sQuery(id+"F0.wireOp",EDGE,"E20"),sQuery(id+"F0.wireOp",EDGE,"E21"),sQuery(id+"F0.wireOp",EDGE,"E22.left"),sQuery(id+"F0.wireOp",EDGE,"E22.right"),sQuery(id+"F0.wireOp",EDGE,"E24.filletArc"),sQuery(id+"F0.wireOp",EDGE,"E25"),sQuery(id+"F0.wireOp",EDGE,"E26.MirrorCS"),sQuery(id+"F0.wireOp",EDGE,"E27.trimOffspring"),sQuery(id+"F0.wireOp",EDGE,"E28.filletArc"),sQuery(id+"F0.wireOp",EDGE,"E29.filletArc"),sQuery(id+"F0.wireOp",EDGE,"E30"),sQuery(id+"F0.wireOp",EDGE,"E31.filletArc"),sQuery(id+"F0.wireOp",EDGE,"E32.filletArc"),sQuery(id+"F0.wireOp",EDGE,"E33"),sQuery(id+"F0.wireOp",EDGE,"E34.filletArc"),sQuery(id+"F0.wireOp",EDGE,"E35.filletArc"),sQuery(id+"F0.wireOp",EDGE,"E36.filletArc"),sQuery(id+"F0.wireOp",EDGE,"E37.MirrorC"),sQuery(id+"F0.wireOp",EDGE,"E38.MirrorC"),sQuery(id+"F0.wireOp",EDGE,"E39.MirrorCS"),sQuery(id+"F0.wireOp",EDGE,"E40.MirrorCS"),sQuery(id+"F0.wireOp",EDGE,"E44.MirrorCS"),sQuery(id+"F0.wireOp",EDGE,"E45.MirrorCS"),sQuery(id+"F0.wireOp",EDGE,"E46.MirrorCS"),sQuery(id+"F0.wireOp",EDGE,"E47.MirrorCS"),sQuery(id+"F0.wireOp",EDGE,"E48.MirrorCS"),sQuery(id+"F0.wireOp",EDGE,"E49.MirrorCS"),sQuery(id+"F0.wireOp",EDGE,"E50.MirrorCS"),sQuery(id+"F0.wireOp",EDGE,"E51.MirrorCS"),sQuery(id+"F0.wireOp",EDGE,"E52.MirrorCS"),sQuery(id+"F0.wireOp",EDGE,"E53.MirrorCS"),sQuery(id+"F0.wireOp",EDGE,"E54.MirrorCS"),sQuery(id+"F0.wireOp",EDGE,"E55.MirrorCS"),sQuery(id+"F0.wireOp",EDGE,"E56.MirrorCS"),sQuery(id+"F0.wireOp",EDGE,"E57.MirrorCS"),sQuery(id+"F0.wireOp",EDGE,"E58.MirrorCS"),sQuery(id+"F0.wireOp",EDGE,"E59.MirrorCS"),sQuery(id+"F0.wireOp",EDGE,"E60.MirrorCS"),sQuery(id+"F0.wireOp",EDGE,"E61.MirrorCS"),sQuery(id+"F0.wireOp",EDGE,"E62.MirrorCS"),sQuery(id+"F0.wireOp",EDGE,"E63.MirrorCS"),sQuery(id+"F0.wireOp",EDGE,"E65.MirrorCS"),sQuery(id+"F0.wireOp",EDGE,"E66.MirrorC"),sQuery(id+"F0.wireOp",EDGE,"E67.MirrorC"),sQuery(id+"F0.wireOp",EDGE,"E68.MirrorCS"),sQuery(id+"F0.wireOp",EDGE,"E69.MirrorCS"),sQuery(id+"F0.wireOp",EDGE,"E70.MirrorCS"),sQuery(id+"F0.wireOp",EDGE,"E71.MirrorCS"),sQuery(id+"F0.wireOp",EDGE,"E72.MirrorCS"),sQuery(id+"F0.wireOp",EDGE,"E73.MirrorCS"),sQuery(id+"F0.wireOp",EDGE,"E74.MirrorCS"),sQuery(id+"F0.wireOp",EDGE,"E75.MirrorCS"),sQuery(id+"F0.wireOp",EDGE,"E76.MirrorCS"),sQuery(id+"F0.wireOp",EDGE,"E77.MirrorCS"),sQuery(id+"F0.wireOp",EDGE,"E78.MirrorCS"),sQuery(id+"F0.wireOp",EDGE,"E79.MirrorCS"),sQuery(id+"F0.wireOp",EDGE,"E80.MirrorCS"),sQuery(id+"F0.wireOp",EDGE,"E81.MirrorCS"),sQuery(id+"F0.wireOp",EDGE,"E82.MirrorCS"),sQuery(id+"F0.wireOp",EDGE,"E83.MirrorCS"),sQuery(id+"F0.wireOp",EDGE,"E84.MirrorCS"),sQuery(id+"F0.wireOp",EDGE,"E85.MirrorCS"),sQuery(id+"F0.wireOp",EDGE,"E86.MirrorCS"),sQuery(id+"F0.wireOp",EDGE,"E87.MirrorC"),sQuery(id+"F0.wireOp",EDGE,"E89.MirrorCS"),sQuery(id+"F0.wireOp",EDGE,"E90.MirrorC"),sQuery(id+"F0.wireOp",EDGE,"E91.MirrorCS"),sQuery(id+"F0.wireOp",EDGE,"E92.MirrorCS"),sQuery(id+"F0.wireOp",EDGE,"E93.MirrorCS"),sQuery(id+"F0.wireOp",EDGE,"E94.MirrorCS"),sQuery(id+"F0.wireOp",EDGE,"E95.MirrorCS"),sQuery(id+"F0.wireOp",EDGE,"E96.MirrorCS"),sQuery(id+"F0.wireOp",EDGE,"E97.MirrorCS"),sQuery(id+"F0.wireOp",EDGE,"E99.MirrorCS"),sQuery(id+"F0.wireOp",EDGE,"E100.MirrorC"),sQuery(id+"F0.wireOp",EDGE,"E101.MirrorCS"),sQuery(id+"F0.wireOp",EDGE,"E102.MirrorCS"),sQuery(id+"F0.wireOp",EDGE,"E105.MirrorCS"),sQuery(id+"F0.wireOp",EDGE,"E106.MirrorCS"),sQuery(id+"F0.wireOp",EDGE,"E108.MirrorCS"),sQuery(id+"F0.wireOp",EDGE,"E109.MirrorC"),sQuery(id+"F0.wireOp",EDGE,"E111.MirrorCS"),sQuery(id+"F0.wireOp",EDGE,"E113.MirrorCS"),sQuery(id+"F0.wireOp",EDGE,"E117.MirrorCS"),sQuery(id+"F0.wireOp",EDGE,"E118.MirrorCS"),sQuery(id+"F0.wireOp",EDGE,"E119.MirrorCS"),sQuery(id+"F0.wireOp",EDGE,"E120.MirrorCS"),sQuery(id+"F0.wireOp",EDGE,"E121.MirrorCS"),sQuery(id+"F0.wireOp",EDGE,"E122.MirrorC"),sQuery(id+"F0.wireOp",EDGE,"E123.MirrorC"),sQuery(id+"F0.wireOp",EDGE,"E127.MirrorCS"),sQuery(id+"F0.wireOp",EDGE,"E128.MirrorCS"),sQuery(id+"F0.wireOp",EDGE,"E129.MirrorCS"),sQuery(id+"F0.wireOp",EDGE,"E130.MirrorCS"),sQuery(id+"F0.wireOp",EDGE,"E131.MirrorCS"),sQuery(id+"F0.wireOp",EDGE,"E133.MirrorCS"),sQuery(id+"F0.wireOp",EDGE,"E135.MirrorCS"),sQuery(id+"F0.wireOp",EDGE,"E136.MirrorCS"),sQuery(id+"F0.wireOp",EDGE,"E138.MirrorCS"),sQuery(id+"F0.wireOp",EDGE,"E139.MirrorCS"),sQuery(id+"F0.wireOp",EDGE,"E140"),sQuery(id+"F0.wireOp",EDGE,"E141.MirrorC"),sQuery(id+"F0.wireOp",EDGE,"E142"),sQuery(id+"F0.wireOp",EDGE,"E143"),sQuery(id+"F0.wireOp",EDGE,"E144.filletArc")])],"isStart":true});
            var sketch = newSketch(context, id + "F7", { "sketchPlane" : qUnion([Q0])});
            skEllipse(sketch, "E222", {"center": v(0, 0) * mm, "majorRadius": 15 * mm, "minorRadius": 7.5 * mm, "majorAxis": v(0, 1)});
            skSolve(sketch);
        }
        {
            var Q0;
            Q0 = qSketchRegion(id + "F7", true);
            extrude(context, id + "F8", {"entities" : qUnion([Q0]), "operationType" : NewBodyOperationType.REMOVE, "oppositeDirection" : true, "depth" : 25 * mm});
        }
        {
            var Q0;
            Q0=qCreatedBy(makeId("Top.planeOp"),FACE);
            var sketch = newSketch(context, id + "F9", { "sketchPlane" : qUnion([Q0])});
            skCircle(sketch, "E223", {"center": v(-12.5, 50) * mm, "radius": 1.75 * mm});
            skCircle(sketch, "E224", {"center": v(-14.5, -28) * mm, "radius": 1.75 * mm});
            skLineSegment(sketch, "E225", {"start": v(-14, 55) * mm, "end": v(-10, 55) * mm});
            skLineSegment(sketch, "E226", {"start": v(-9, 54) * mm, "end": v(-9, 37) * mm});
            skLineSegment(sketch, "E227", {"start": v(-6, 34) * mm, "end": v(0, 34) * mm});
            skPoint(sketch, "E228.visualSharp", {"position": v(-17, 55) * mm});
            skArc(sketch, "E228.filletArc", {"start": v(-14, 55) * mm, "mid": v(-16.12, 54.12) * mm, "end": v(-17, 52) * mm});
            skPoint(sketch, "E229.visualSharp", {"position": v(-9, 55) * mm});
            skArc(sketch, "E229.filletArc", {"start": v(-9, 54) * mm, "mid": v(-9.3, 54.7) * mm, "end": v(-10, 55) * mm});
            skPoint(sketch, "E230.visualSharp", {"position": v(-9, 34) * mm});
            skArc(sketch, "E230.filletArc", {"start": v(-9, 37) * mm, "mid": v(-8.12, 34.88) * mm, "end": v(-6, 34) * mm});
            skArc(sketch, "E231.MirrorCS", {"start": v(9, 54) * mm, "mid": v(9.3, 54.7) * mm, "end": v(10, 55) * mm});
            skArc(sketch, "E232.MirrorCS", {"start": v(9, 37) * mm, "mid": v(8.12, 34.88) * mm, "end": v(6, 34) * mm});
            skArc(sketch, "E233.MirrorCS", {"start": v(14, 55) * mm, "mid": v(16.12, 54.12) * mm, "end": v(17, 52) * mm});
            skLineSegment(sketch, "E234.MirrorCS", {"start": v(14, 55) * mm, "end": v(10, 55) * mm});
            skCircle(sketch, "E235.MirrorC", {"center": v(12.5, 50) * mm, "radius": 1.75 * mm});
            skPoint(sketch, "E236.MirrorP", {"position": v(9, 55) * mm});
            skPoint(sketch, "E237.MirrorP", {"position": v(9, 34) * mm});
            skLineSegment(sketch, "E238.MirrorCS", {"start": v(9, 54) * mm, "end": v(9, 37) * mm});
            skPoint(sketch, "E239.MirrorP", {"position": v(17, 55) * mm});
            skCircle(sketch, "E240.MirrorC", {"center": v(14.5, -28) * mm, "radius": 1.75 * mm});
            skLineSegment(sketch, "E241.MirrorCS", {"start": v(6, 34) * mm, "end": v(0, 34) * mm});
            skLineSegment(sketch, "E242.bottom", {"start": v(-19, 18) * mm, "end": v(-19, 18) * mm});
            skLineSegment(sketch, "E242.top", {"start": v(-19, -18) * mm, "end": v(-19, -18) * mm});
            skLineSegment(sketch, "E242.left", {"start": v(-19, 18) * mm, "end": v(-19, -18) * mm});
            skLineSegment(sketch, "E242.right", {"start": v(19, 18) * mm, "end": v(19, -18) * mm});
            skPoint(sketch, "E242.middle", {"position": v(0, 0) * mm});
            skLineSegment(sketch, "E243", {"start": v(-17, 52) * mm, "end": v(-17, 20) * mm});
            skLineSegment(sketch, "E244", {"start": v(17, 52) * mm, "end": v(17, 20) * mm});
            skLineSegment(sketch, "E245.trimOffspring", {"start": v(19, 18) * mm, "end": v(19, 18) * mm});
            skArc(sketch, "E246", {"start": v(-17.62, -24.75) * mm, "mid": v(-18.02, -30.8) * mm, "end": v(-12.04, -31.77) * mm});
            skArc(sketch, "E247", {"start": v(12.04, -31.77) * mm, "mid": v(18.02, -30.8) * mm, "end": v(17.62, -24.75) * mm});
            skLineSegment(sketch, "E248", {"start": v(-17, -20) * mm, "end": v(-17, -23.3) * mm});
            skLineSegment(sketch, "E249.MirrorCS", {"start": v(17, -20) * mm, "end": v(17, -23.3) * mm});
            skLineSegment(sketch, "E250.trimOffspring", {"start": v(19, -18) * mm, "end": v(19, -18) * mm});
            skArc(sketch, "E251", {"start": v(12.04, -31.77) * mm, "mid": v(11.12, -31.2) * mm, "end": v(10.18, -30.68) * mm});
            skPoint(sketch, "E252.visualSharp", {"position": v(-17, 18) * mm});
            skArc(sketch, "E252.filletArc", {"start": v(-19, 18) * mm, "mid": v(-17.59, 18.59) * mm, "end": v(-17, 20) * mm});
            skPoint(sketch, "E253.visualSharp", {"position": v(-17, -18) * mm});
            skArc(sketch, "E253.filletArc", {"start": v(-17, -20) * mm, "mid": v(-17.59, -18.59) * mm, "end": v(-19, -18) * mm});
            skPoint(sketch, "E254.visualSharp", {"position": v(-17, -24.26) * mm});
            skArc(sketch, "E254.filletArc", {"start": v(-17.62, -24.75) * mm, "mid": v(-17.16, -24.1) * mm, "end": v(-17, -23.3) * mm});
            skPoint(sketch, "E255.visualSharp", {"position": v(17, -18) * mm});
            skArc(sketch, "E255.filletArc", {"start": v(19, -18) * mm, "mid": v(17.59, -18.59) * mm, "end": v(17, -20) * mm});
            skPoint(sketch, "E256.visualSharp", {"position": v(17, -24.26) * mm});
            skArc(sketch, "E256.filletArc", {"start": v(17, -23.3) * mm, "mid": v(17.16, -24.1) * mm, "end": v(17.62, -24.75) * mm});
            skPoint(sketch, "E257.visualSharp", {"position": v(17, 18) * mm});
            skArc(sketch, "E257.filletArc", {"start": v(17, 20) * mm, "mid": v(17.59, 18.59) * mm, "end": v(19, 18) * mm});
            skCircle(sketch, "E258", {"center": v(0, -31.43) * mm, "radius": 3.25 * mm});
            skArc(sketch, "E259", {"start": v(-5.86, -32.7) * mm, "mid": v(0, -37.43) * mm, "end": v(5.86, -32.7) * mm});
            skArc(sketch, "E260.trimOffspring", {"start": v(-10.18, -30.68) * mm, "mid": v(-11.12, -31.2) * mm, "end": v(-12.04, -31.77) * mm});
            skPoint(sketch, "E261.visualSharp", {"position": v(-5.42, -28.86) * mm});
            skArc(sketch, "E261.filletArc", {"start": v(-5.86, -32.7) * mm, "mid": v(-7.52, -30.62) * mm, "end": v(-10.18, -30.68) * mm});
            skPoint(sketch, "E262.visualSharp", {"position": v(5.42, -28.86) * mm});
            skArc(sketch, "E262.filletArc", {"start": v(10.18, -30.68) * mm, "mid": v(7.52, -30.62) * mm, "end": v(5.86, -32.7) * mm});
            skSolve(sketch);
        }
        {
            var Q0;
            Q0=makeQuery(id+"F9.imprint","IMPRINT",FACE,{"disambiguationData":[TD([[makeQuery(id+"F9.imprint","IMPRINT",EDGE,{"derivedFrom":sQuery(id+"F9.wireOp",EDGE,"E223")}),-1.0]])]});
            extrude(context, id + "F10", {"entities" : qUnion([Q0]), "depth" : 2 * mm});
        }
        {
            var Q0;
            Q0=qCreatedBy(makeId("Top.planeOp"),FACE);
            var sketch = newSketch(context, id + "F11", { "sketchPlane" : qUnion([Q0])});
            skCircle(sketch, "E263", {"center": v(0, 0) * mm, "radius": 1.25 * mm});
            skCircle(sketch, "E264", {"center": v(0, 0) * mm, "radius": 2.75 * mm});
            skSolve(sketch);
        }
        {
            var Q0;
            Q0=makeQuery(id+"F11.imprint","IMPRINT",FACE,{"disambiguationData":[TD([[makeQuery(id+"F11.imprint","IMPRINT",EDGE,{"derivedFrom":sQuery(id+"F11.wireOp",EDGE,"E263")}),-1.0]])]});
            extrude(context, id + "F12", {"entities" : qUnion([Q0]), "depth" : 35 * mm});
        }
        {
            var Q0;
            Q0=makeQuery(id+"F10.opExtrude","SWEPT_EDGE",EDGE,{"disambiguationData":[OSD([sQuery(id+"F9.wireOp",EDGE,"E242.left"),sQuery(id+"F9.wireOp",EDGE,"E253.filletArc")])]});
            var Q1;
            Q1=makeQuery(id+"F10.opExtrude","SWEPT_EDGE",EDGE,{"disambiguationData":[OSD([sQuery(id+"F9.wireOp",EDGE,"E242.left"),sQuery(id+"F9.wireOp",EDGE,"E252.filletArc")])]});
            var Q2;
            Q2=makeQuery(id+"F10.opExtrude","SWEPT_EDGE",EDGE,{"disambiguationData":[OSD([sQuery(id+"F9.wireOp",EDGE,"E242.right"),sQuery(id+"F9.wireOp",EDGE,"E257.filletArc")])]});
            var Q3;
            Q3=makeQuery(id+"F10.opExtrude","SWEPT_EDGE",EDGE,{"disambiguationData":[OSD([sQuery(id+"F9.wireOp",EDGE,"E242.right"),sQuery(id+"F9.wireOp",EDGE,"E255.filletArc")])]});
            fillet(context, id + "F13", {"entities" : qUnion([Q0, Q1, Q2, Q3]), "radius" : 3 * mm, "tangentPropagation" : true, "allowEdgeOverflow" : false});
        }
        {
            var Q0;
            Q0=makeQuery(id+"F10.opExtrude","CAP_FACE",FACE,{"disambiguationData":[OSD([sQuery(id+"F9.wireOp",EDGE,"E223"),sQuery(id+"F9.wireOp",EDGE,"E224"),sQuery(id+"F9.wireOp",EDGE,"E225"),sQuery(id+"F9.wireOp",EDGE,"E226"),sQuery(id+"F9.wireOp",EDGE,"E227"),sQuery(id+"F9.wireOp",EDGE,"E228.filletArc"),sQuery(id+"F9.wireOp",EDGE,"E229.filletArc"),sQuery(id+"F9.wireOp",EDGE,"E230.filletArc"),sQuery(id+"F9.wireOp",EDGE,"E231.MirrorCS"),sQuery(id+"F9.wireOp",EDGE,"E232.MirrorCS"),sQuery(id+"F9.wireOp",EDGE,"E233.MirrorCS"),sQuery(id+"F9.wireOp",EDGE,"E234.MirrorCS"),sQuery(id+"F9.wireOp",EDGE,"E235.MirrorC"),sQuery(id+"F9.wireOp",EDGE,"E238.MirrorCS"),sQuery(id+"F9.wireOp",EDGE,"E240.MirrorC"),sQuery(id+"F9.wireOp",EDGE,"E241.MirrorCS"),sQuery(id+"F9.wireOp",EDGE,"E242.left"),sQuery(id+"F9.wireOp",EDGE,"E242.right"),sQuery(id+"F9.wireOp",EDGE,"E243"),sQuery(id+"F9.wireOp",EDGE,"E244"),sQuery(id+"F9.wireOp",EDGE,"E246"),sQuery(id+"F9.wireOp",EDGE,"E247"),sQuery(id+"F9.wireOp",EDGE,"E248"),sQuery(id+"F9.wireOp",EDGE,"E249.MirrorCS"),sQuery(id+"F9.wireOp",EDGE,"E251"),sQuery(id+"F9.wireOp",EDGE,"E252.filletArc"),sQuery(id+"F9.wireOp",EDGE,"E253.filletArc"),sQuery(id+"F9.wireOp",EDGE,"E254.filletArc"),sQuery(id+"F9.wireOp",EDGE,"E255.filletArc"),sQuery(id+"F9.wireOp",EDGE,"E256.filletArc"),sQuery(id+"F9.wireOp",EDGE,"E257.filletArc")])],"isStart":false});
            var sketch = newSketch(context, id + "F14", { "sketchPlane" : qUnion([Q0])});
            skLineSegment(sketch, "E265.bottom", {"start": v(6, 16) * mm, "end": v(-6, 16) * mm});
            skLineSegment(sketch, "E265.top", {"start": v(6, 28) * mm, "end": v(-6, 28) * mm});
            skLineSegment(sketch, "E265.left", {"start": v(9, 19) * mm, "end": v(9, 25) * mm});
            skLineSegment(sketch, "E265.right", {"start": v(-9, 19) * mm, "end": v(-9, 25) * mm});
            skPoint(sketch, "E265.middle", {"position": v(0, 22) * mm});
            skLineSegment(sketch, "E266.bottom", {"start": v(6, -3) * mm, "end": v(-6, -3) * mm});
            skLineSegment(sketch, "E266.top", {"start": v(6, 7) * mm, "end": v(-6, 7) * mm});
            skLineSegment(sketch, "E266.left", {"start": v(9, 0) * mm, "end": v(9, 4) * mm});
            skLineSegment(sketch, "E266.right", {"start": v(-9, 0) * mm, "end": v(-9, 4) * mm});
            skPoint(sketch, "E266.middle", {"position": v(0, 2) * mm});
            skLineSegment(sketch, "E267", {"start": v(0, -24.5) * mm, "end": v(0, -22) * mm, "construction": true});
            skLineSegment(sketch, "E268", {"start": v(6, -24.5) * mm, "end": v(6, -22) * mm, "construction": true});
            skArc(sketch, "E269.0.startCap", {"start": v(7.25, -24.5) * mm, "mid": v(6, -25.75) * mm, "end": v(4.75, -24.5) * mm});
            skArc(sketch, "E269.0.endCap", {"start": v(4.75, -22) * mm, "mid": v(6, -20.75) * mm, "end": v(7.25, -22) * mm});
            skLineSegment(sketch, "E269.0.left", {"start": v(4.75, -24.5) * mm, "end": v(4.75, -22) * mm});
            skLineSegment(sketch, "E269.0.right", {"start": v(7.25, -24.5) * mm, "end": v(7.25, -22) * mm});
            skArc(sketch, "E270.0.startCap", {"start": v(1.25, -24.5) * mm, "mid": v(0, -25.75) * mm, "end": v(-1.25, -24.5) * mm});
            skArc(sketch, "E270.0.endCap", {"start": v(-1.25, -22) * mm, "mid": v(0, -20.75) * mm, "end": v(1.25, -22) * mm});
            skLineSegment(sketch, "E270.0.left", {"start": v(-1.25, -24.5) * mm, "end": v(-1.25, -22) * mm});
            skLineSegment(sketch, "E270.0.right", {"start": v(1.25, -24.5) * mm, "end": v(1.25, -22) * mm});
            skArc(sketch, "E271.MirrorCS", {"start": v(-4.75, -22) * mm, "mid": v(-6, -20.75) * mm, "end": v(-7.25, -22) * mm});
            skLineSegment(sketch, "E272.MirrorCS", {"start": v(-7.25, -24.5) * mm, "end": v(-7.25, -22) * mm});
            skLineSegment(sketch, "E273.MirrorCS", {"start": v(-4.75, -24.5) * mm, "end": v(-4.75, -22) * mm});
            skArc(sketch, "E274.MirrorCS", {"start": v(-7.25, -24.5) * mm, "mid": v(-6, -25.75) * mm, "end": v(-4.75, -24.5) * mm});
            skLineSegment(sketch, "E275", {"start": v(-14.6, -19.75) * mm, "end": v(14.6, -19.75) * mm, "construction": true});
            skLineSegment(sketch, "E276.MirrorCS", {"start": v(6, -15) * mm, "end": v(6, -17.5) * mm, "construction": true});
            skLineSegment(sketch, "E277.MirrorCS", {"start": v(0, -15) * mm, "end": v(0, -17.5) * mm, "construction": true});
            skLineSegment(sketch, "E278.MirrorCS", {"start": v(-1.25, -15) * mm, "end": v(-1.25, -17.5) * mm});
            skLineSegment(sketch, "E279.MirrorCS", {"start": v(1.25, -15) * mm, "end": v(1.25, -17.5) * mm});
            skArc(sketch, "E280.MirrorCS", {"start": v(-1.25, -17.5) * mm, "mid": v(0, -18.75) * mm, "end": v(1.25, -17.5) * mm});
            skArc(sketch, "E281.MirrorCS", {"start": v(-7.25, -15) * mm, "mid": v(-6, -13.75) * mm, "end": v(-4.75, -15) * mm});
            skArc(sketch, "E282.MirrorCS", {"start": v(1.25, -15) * mm, "mid": v(0, -13.75) * mm, "end": v(-1.25, -15) * mm});
            skArc(sketch, "E283.MirrorCS", {"start": v(-4.75, -17.5) * mm, "mid": v(-6, -18.75) * mm, "end": v(-7.25, -17.5) * mm});
            skLineSegment(sketch, "E284.MirrorCS", {"start": v(4.75, -15) * mm, "end": v(4.75, -17.5) * mm});
            skLineSegment(sketch, "E285.MirrorCS", {"start": v(7.25, -15) * mm, "end": v(7.25, -17.5) * mm});
            skLineSegment(sketch, "E286.MirrorCS", {"start": v(-7.25, -15) * mm, "end": v(-7.25, -17.5) * mm});
            skLineSegment(sketch, "E287.MirrorCS", {"start": v(-4.75, -15) * mm, "end": v(-4.75, -17.5) * mm});
            skArc(sketch, "E288.MirrorCS", {"start": v(4.75, -17.5) * mm, "mid": v(6, -18.75) * mm, "end": v(7.25, -17.5) * mm});
            skArc(sketch, "E289.MirrorCS", {"start": v(7.25, -15) * mm, "mid": v(6, -13.75) * mm, "end": v(4.75, -15) * mm});
            skLineSegment(sketch, "E290", {"start": v(-14.5, -5.75) * mm, "end": v(-14.5, -3.25) * mm, "construction": true});
            skLineSegment(sketch, "E291", {"start": v(-14.5, 3.25) * mm, "end": v(-14.5, 5.75) * mm, "construction": true});
            skArc(sketch, "E292.0.startCap", {"start": v(-13.25, 3.25) * mm, "mid": v(-14.5, 2) * mm, "end": v(-15.75, 3.25) * mm});
            skArc(sketch, "E292.0.endCap", {"start": v(-15.75, 5.75) * mm, "mid": v(-14.5, 7) * mm, "end": v(-13.25, 5.75) * mm});
            skLineSegment(sketch, "E292.0.left", {"start": v(-15.75, 3.25) * mm, "end": v(-15.75, 5.75) * mm});
            skLineSegment(sketch, "E292.0.right", {"start": v(-13.25, 3.25) * mm, "end": v(-13.25, 5.75) * mm});
            skArc(sketch, "E292.1.startCap", {"start": v(-13.25, -5.75) * mm, "mid": v(-14.5, -7) * mm, "end": v(-15.75, -5.75) * mm});
            skArc(sketch, "E292.1.endCap", {"start": v(-15.75, -3.25) * mm, "mid": v(-14.5, -2) * mm, "end": v(-13.25, -3.25) * mm});
            skLineSegment(sketch, "E292.1.left", {"start": v(-15.75, -5.75) * mm, "end": v(-15.75, -3.25) * mm});
            skLineSegment(sketch, "E292.1.right", {"start": v(-13.25, -5.75) * mm, "end": v(-13.25, -3.25) * mm});
            skLineSegment(sketch, "E293", {"start": v(-14.5, 12.25) * mm, "end": v(-14.5, 14.75) * mm, "construction": true});
            skArc(sketch, "E294.0.startCap", {"start": v(-13.25, 12.25) * mm, "mid": v(-14.5, 11) * mm, "end": v(-15.75, 12.25) * mm});
            skArc(sketch, "E294.0.endCap", {"start": v(-15.75, 14.75) * mm, "mid": v(-14.5, 16) * mm, "end": v(-13.25, 14.75) * mm});
            skLineSegment(sketch, "E294.0.left", {"start": v(-15.75, 12.25) * mm, "end": v(-15.75, 14.75) * mm});
            skLineSegment(sketch, "E294.0.right", {"start": v(-13.25, 12.25) * mm, "end": v(-13.25, 14.75) * mm});
            skArc(sketch, "E295.MirrorCS", {"start": v(13.25, 12.25) * mm, "mid": v(14.5, 11) * mm, "end": v(15.75, 12.25) * mm});
            skLineSegment(sketch, "E296.MirrorCS", {"start": v(13.25, 3.25) * mm, "end": v(13.25, 5.75) * mm});
            skArc(sketch, "E297.MirrorCS", {"start": v(15.75, 5.75) * mm, "mid": v(14.5, 7) * mm, "end": v(13.25, 5.75) * mm});
            skArc(sketch, "E298.MirrorCS", {"start": v(15.75, 14.75) * mm, "mid": v(14.5, 16) * mm, "end": v(13.25, 14.75) * mm});
            skLineSegment(sketch, "E299.MirrorCS", {"start": v(13.25, -5.75) * mm, "end": v(13.25, -3.25) * mm});
            skArc(sketch, "E300.MirrorCS", {"start": v(13.25, 3.25) * mm, "mid": v(14.5, 2) * mm, "end": v(15.75, 3.25) * mm});
            skArc(sketch, "E301.MirrorCS", {"start": v(13.25, -5.75) * mm, "mid": v(14.5, -7) * mm, "end": v(15.75, -5.75) * mm});
            skLineSegment(sketch, "E302.MirrorCS", {"start": v(14.5, 12.25) * mm, "end": v(14.5, 14.75) * mm, "construction": true});
            skLineSegment(sketch, "E303.MirrorCS", {"start": v(15.75, 3.25) * mm, "end": v(15.75, 5.75) * mm});
            skArc(sketch, "E304.MirrorCS", {"start": v(15.75, -3.25) * mm, "mid": v(14.5, -2) * mm, "end": v(13.25, -3.25) * mm});
            skLineSegment(sketch, "E305.MirrorCS", {"start": v(14.5, 3.25) * mm, "end": v(14.5, 5.75) * mm, "construction": true});
            skLineSegment(sketch, "E306.MirrorCS", {"start": v(14.5, -5.75) * mm, "end": v(14.5, -3.25) * mm, "construction": true});
            skLineSegment(sketch, "E307.MirrorCS", {"start": v(15.75, 12.25) * mm, "end": v(15.75, 14.75) * mm});
            skLineSegment(sketch, "E308.MirrorCS", {"start": v(15.75, -5.75) * mm, "end": v(15.75, -3.25) * mm});
            skLineSegment(sketch, "E309.MirrorCS", {"start": v(13.25, 12.25) * mm, "end": v(13.25, 14.75) * mm});
            skPoint(sketch, "E310.visualSharp", {"position": v(-9, 28) * mm});
            skArc(sketch, "E310.filletArc", {"start": v(-6, 28) * mm, "mid": v(-8.12, 27.12) * mm, "end": v(-9, 25) * mm});
            skPoint(sketch, "E311.visualSharp", {"position": v(-9, 16) * mm});
            skArc(sketch, "E311.filletArc", {"start": v(-9, 19) * mm, "mid": v(-8.12, 16.88) * mm, "end": v(-6, 16) * mm});
            skPoint(sketch, "E312.visualSharp", {"position": v(9, 16) * mm});
            skArc(sketch, "E312.filletArc", {"start": v(6, 16) * mm, "mid": v(8.12, 16.88) * mm, "end": v(9, 19) * mm});
            skPoint(sketch, "E313.visualSharp", {"position": v(9, 28) * mm});
            skArc(sketch, "E313.filletArc", {"start": v(9, 25) * mm, "mid": v(8.12, 27.12) * mm, "end": v(6, 28) * mm});
            skPoint(sketch, "E314.visualSharp", {"position": v(-9, 7) * mm});
            skArc(sketch, "E314.filletArc", {"start": v(-6, 7) * mm, "mid": v(-8.12, 6.12) * mm, "end": v(-9, 4) * mm});
            skPoint(sketch, "E315.visualSharp", {"position": v(-9, -3) * mm});
            skArc(sketch, "E315.filletArc", {"start": v(-9, 0) * mm, "mid": v(-8.12, -2.12) * mm, "end": v(-6, -3) * mm});
            skPoint(sketch, "E316.visualSharp", {"position": v(9, -3) * mm});
            skArc(sketch, "E316.filletArc", {"start": v(6, -3) * mm, "mid": v(8.12, -2.12) * mm, "end": v(9, 0) * mm});
            skPoint(sketch, "E317.visualSharp", {"position": v(9, 7) * mm});
            skArc(sketch, "E317.filletArc", {"start": v(9, 4) * mm, "mid": v(8.12, 6.12) * mm, "end": v(6, 7) * mm});
            skSolve(sketch);
        }
        {
            var Q0;
            Q0 = qSketchRegion(id + "F14", true);
            extrude(context, id + "F15", {"entities" : qUnion([Q0]), "operationType" : NewBodyOperationType.REMOVE, "oppositeDirection" : true, "depth" : 25 * mm});
        }
    });
